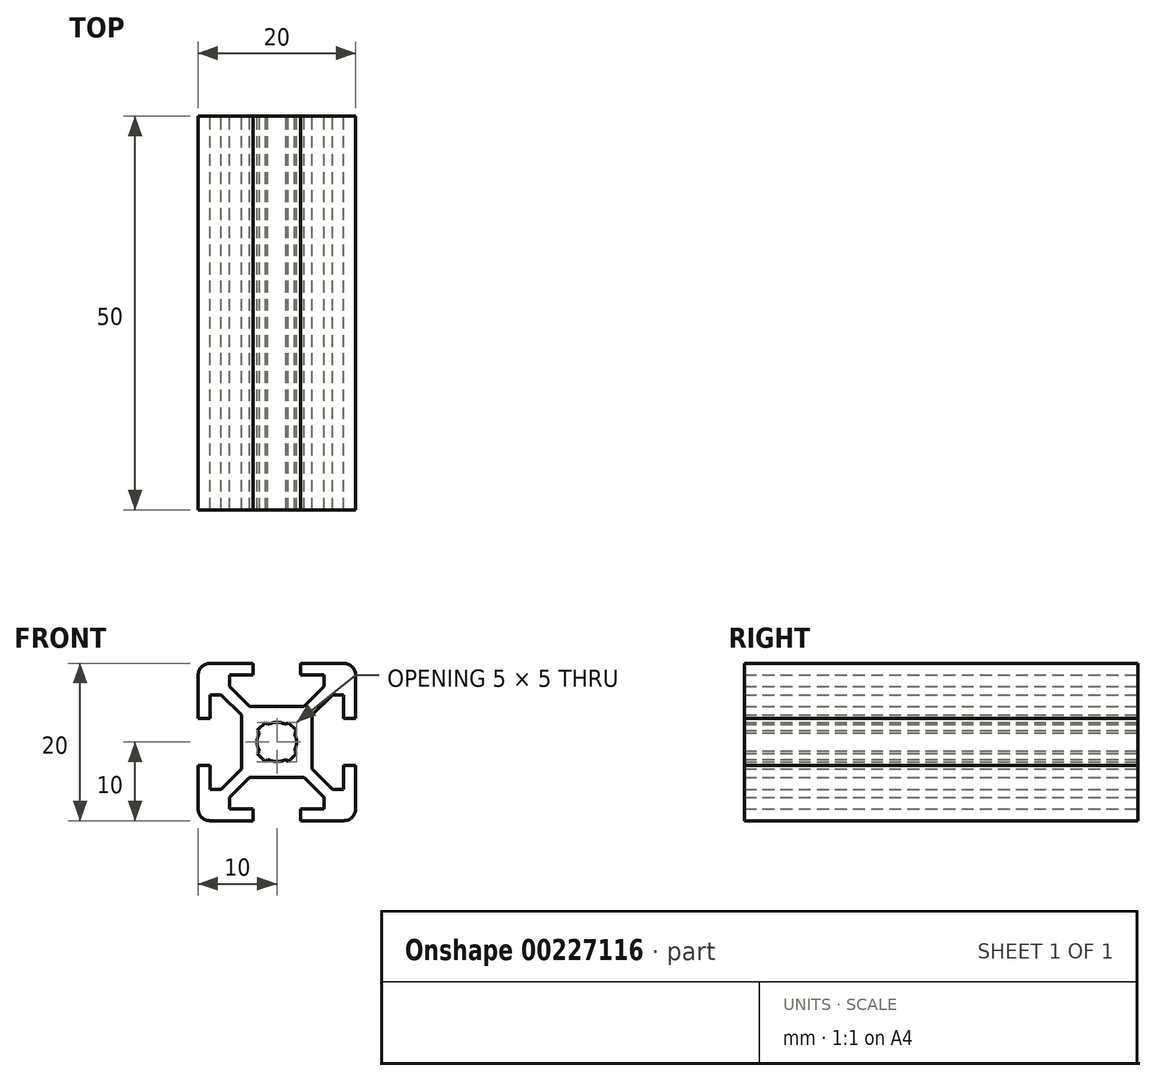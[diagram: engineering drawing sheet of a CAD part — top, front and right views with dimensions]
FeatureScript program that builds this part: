
annotation { "Feature Type Name" : "Feature", "Feature Type Description" : "" }
export const myFeature = defineFeature(function(context is Context, id is Id, definition is map)
    precondition{}
    {
        {
            var Q0;
            Q0=qCreatedBy(makeId("Front.planeOp"),FACE);
            var sketch = newSketch(context, id + "F0", { "sketchPlane" : qUnion([Q0])});
            skLineSegment(sketch, "E0.bottom", {"start": v(8.5, -10) * mm, "end": v(3, -10) * mm});
            skLineSegment(sketch, "E0.top", {"start": v(8.5, 10) * mm, "end": v(3, 10) * mm});
            skLineSegment(sketch, "E0.left", {"start": v(10, -8.5) * mm, "end": v(10, -3) * mm});
            skLineSegment(sketch, "E0.right", {"start": v(-10, -8.5) * mm, "end": v(-10, -3) * mm});
            skPoint(sketch, "E0.middle", {"position": v(0, 0) * mm});
            skLineSegment(sketch, "E1.bottom", {"start": v(6, -8.5) * mm, "end": v(3, -8.5) * mm});
            skLineSegment(sketch, "E1.top", {"start": v(6, 8.5) * mm, "end": v(3, 8.5) * mm});
            skLineSegment(sketch, "E1.left", {"start": v(8.5, -6) * mm, "end": v(8.5, -3) * mm});
            skLineSegment(sketch, "E1.right", {"start": v(-8.5, -6) * mm, "end": v(-8.5, -3) * mm});
            skLineSegment(sketch, "E2.bottom", {"start": v(3.44, -4.5) * mm, "end": v(-3.44, -4.5) * mm});
            skLineSegment(sketch, "E2.top", {"start": v(3.44, 4.5) * mm, "end": v(-3.44, 4.5) * mm});
            skLineSegment(sketch, "E2.left", {"start": v(4.5, -3.44) * mm, "end": v(4.5, 3.44) * mm});
            skLineSegment(sketch, "E2.right", {"start": v(-4.5, -3.44) * mm, "end": v(-4.5, 3.44) * mm});
            skLineSegment(sketch, "E3.bottom", {"start": v(8.5, -6) * mm, "end": v(7.06, -6) * mm});
            skLineSegment(sketch, "E3.top", {"start": v(8.5, 6) * mm, "end": v(7.06, 6) * mm});
            skLineSegment(sketch, "E4.left", {"start": v(6, -8.5) * mm, "end": v(6, -7.06) * mm});
            skLineSegment(sketch, "E4.right", {"start": v(-6, -8.5) * mm, "end": v(-6, -7.06) * mm});
            skPoint(sketch, "E5.orphan", {"position": v(-8.5, 8.5) * mm});
            skPoint(sketch, "E6.orphan", {"position": v(8.5, 8.5) * mm});
            skPoint(sketch, "E7.orphan", {"position": v(8.5, -8.5) * mm});
            skPoint(sketch, "E8.orphan", {"position": v(-8.5, -8.5) * mm});
            skLineSegment(sketch, "E9.trimOffspring", {"start": v(-6, 7.06) * mm, "end": v(-6, 8.5) * mm});
            skLineSegment(sketch, "E10.trimOffspring", {"start": v(-7.06, 6) * mm, "end": v(-8.5, 6) * mm});
            skLineSegment(sketch, "E11.trimOffspring", {"start": v(6, 7.06) * mm, "end": v(6, 8.5) * mm});
            skLineSegment(sketch, "E12.trimOffspring", {"start": v(-7.06, -6) * mm, "end": v(-8.5, -6) * mm});
            skLineSegment(sketch, "E13", {"start": v(-10, 10) * mm, "end": v(0, 0) * mm, "construction": true});
            skLineSegment(sketch, "E14", {"start": v(10, 10) * mm, "end": v(0, 0) * mm, "construction": true});
            skLineSegment(sketch, "E15", {"start": v(-6, 7.06) * mm, "end": v(-3.44, 4.5) * mm});
            skPoint(sketch, "E15.endSnap0", {"position": v(7.25, -6) * mm});
            skLineSegment(sketch, "E16", {"start": v(6, -7.06) * mm, "end": v(3.44, -4.5) * mm});
            skLineSegment(sketch, "E17", {"start": v(7.06, 6) * mm, "end": v(4.5, 3.44) * mm});
            skLineSegment(sketch, "E18", {"start": v(6, 7.06) * mm, "end": v(3.44, 4.5) * mm});
            skPoint(sketch, "E19.orphan", {"position": v(6, -6) * mm});
            skPoint(sketch, "E20.orphan", {"position": v(-4.5, -4.5) * mm});
            skPoint(sketch, "E21.orphan", {"position": v(-4.5, 4.5) * mm});
            skPoint(sketch, "E22.orphan", {"position": v(4.5, 4.5) * mm});
            skPoint(sketch, "E23.orphan", {"position": v(4.5, -4.5) * mm});
            skLineSegment(sketch, "E24.trimOffspring", {"start": v(4.5, -3.44) * mm, "end": v(7.06, -6) * mm});
            skLineSegment(sketch, "E25.trimOffspring", {"start": v(-3.44, -4.5) * mm, "end": v(-6, -7.06) * mm});
            skLineSegment(sketch, "E26.trimOffspring", {"start": v(-4.5, -3.44) * mm, "end": v(-7.06, -6) * mm});
            skLineSegment(sketch, "E27.trimOffspring", {"start": v(-4.5, 3.44) * mm, "end": v(-7.06, 6) * mm});
            skLineSegment(sketch, "E28.bottom", {"start": v(8.5, -3) * mm, "end": v(10, -3) * mm});
            skLineSegment(sketch, "E28.top", {"start": v(8.5, 3) * mm, "end": v(10, 3) * mm});
            skPoint(sketch, "E28.middle", {"position": v(10, 0) * mm});
            skLineSegment(sketch, "E29.left", {"start": v(3, 8.5) * mm, "end": v(3, 10) * mm});
            skLineSegment(sketch, "E29.right", {"start": v(-3, 8.5) * mm, "end": v(-3, 10) * mm});
            skPoint(sketch, "E29.middle", {"position": v(0, 10) * mm});
            skLineSegment(sketch, "E30.bottom", {"start": v(-8.5, 3) * mm, "end": v(-10, 3) * mm});
            skLineSegment(sketch, "E30.top", {"start": v(-8.5, -3) * mm, "end": v(-10, -3) * mm});
            skPoint(sketch, "E30.middle", {"position": v(-10, 0) * mm});
            skLineSegment(sketch, "E31.left", {"start": v(3, -8.5) * mm, "end": v(3, -10) * mm});
            skLineSegment(sketch, "E31.right", {"start": v(-3, -8.5) * mm, "end": v(-3, -10) * mm});
            skPoint(sketch, "E31.middle", {"position": v(0, -10) * mm});
            skPoint(sketch, "E32.orphan", {"position": v(3, 11.5) * mm});
            skPoint(sketch, "E33.orphan", {"position": v(-3, 11.5) * mm});
            skLineSegment(sketch, "E34.trimOffspring", {"start": v(-3, 10) * mm, "end": v(-8.5, 10) * mm});
            skLineSegment(sketch, "E35.trimOffspring", {"start": v(-3, 8.5) * mm, "end": v(-6, 8.5) * mm});
            skPoint(sketch, "E28.right.end.orphan", {"position": v(11.5, 3) * mm});
            skPoint(sketch, "E36.orphan", {"position": v(11.5, -3) * mm});
            skLineSegment(sketch, "E37.trimOffspring", {"start": v(10, 3) * mm, "end": v(10, 8.5) * mm});
            skLineSegment(sketch, "E38.trimOffspring", {"start": v(8.5, 3) * mm, "end": v(8.5, 6) * mm});
            skPoint(sketch, "E39.orphan", {"position": v(3, -11.5) * mm});
            skPoint(sketch, "E40.orphan", {"position": v(-3, -11.5) * mm});
            skLineSegment(sketch, "E41.trimOffspring", {"start": v(-3, -10) * mm, "end": v(-8.5, -10) * mm});
            skLineSegment(sketch, "E42.trimOffspring", {"start": v(-3, -8.5) * mm, "end": v(-6, -8.5) * mm});
            skPoint(sketch, "E30.right.end.orphan", {"position": v(-11.5, -3) * mm});
            skPoint(sketch, "E43.orphan", {"position": v(-11.5, 3) * mm});
            skLineSegment(sketch, "E44.trimOffspring", {"start": v(-10, 3) * mm, "end": v(-10, 8.5) * mm});
            skLineSegment(sketch, "E45.trimOffspring", {"start": v(-8.5, 3) * mm, "end": v(-8.5, 6) * mm});
            skLineSegment(sketch, "E46.trimOffspring", {"start": v(0, 0) * mm, "end": v(10, -10) * mm, "construction": true});
            skLineSegment(sketch, "E47.trimOffspring", {"start": v(0, 0) * mm, "end": v(-10, -10) * mm, "construction": true});
            skArc(sketch, "E48", {"start": v(1.16, 2.22) * mm, "mid": v(0, 2.5) * mm, "end": v(-1.16, 2.22) * mm});
            skLineSegment(sketch, "E49", {"start": v(-2.5, -1.44) * mm, "end": v(1.44, 2.5) * mm});
            skLineSegment(sketch, "E50", {"start": v(2.5, 1.44) * mm, "end": v(-1.44, -2.5) * mm});
            skLineSegment(sketch, "E51", {"start": v(1.44, -2.5) * mm, "end": v(-2.5, 1.44) * mm});
            skLineSegment(sketch, "E52", {"start": v(-1.44, 2.5) * mm, "end": v(2.5, -1.44) * mm});
            skLineSegment(sketch, "E53", {"start": v(2.5, 1.44) * mm, "end": v(2.5, -1.44) * mm, "construction": true});
            skLineSegment(sketch, "E54", {"start": v(1.44, -2.5) * mm, "end": v(-1.44, -2.5) * mm, "construction": true});
            skLineSegment(sketch, "E55", {"start": v(-2.5, -1.44) * mm, "end": v(-2.5, 1.44) * mm, "construction": true});
            skLineSegment(sketch, "E56", {"start": v(-1.44, 2.5) * mm, "end": v(1.44, 2.5) * mm, "construction": true});
            skLineSegment(sketch, "E57", {"start": v(-1.44, 2.5) * mm, "end": v(-2.5, 1.44) * mm});
            skLineSegment(sketch, "E58", {"start": v(1.44, 2.5) * mm, "end": v(2.5, 1.44) * mm});
            skLineSegment(sketch, "E59", {"start": v(2.5, -1.44) * mm, "end": v(1.44, -2.5) * mm});
            skLineSegment(sketch, "E60", {"start": v(-1.44, -2.5) * mm, "end": v(-2.5, -1.44) * mm});
            skArc(sketch, "E61.trimOffspring", {"start": v(-2.22, 1.16) * mm, "mid": v(-2.5, 0) * mm, "end": v(-2.22, -1.16) * mm});
            skArc(sketch, "E62.trimOffspring", {"start": v(-1.16, -2.22) * mm, "mid": v(0, -2.5) * mm, "end": v(1.16, -2.22) * mm});
            skArc(sketch, "E63.trimOffspring", {"start": v(2.22, -1.16) * mm, "mid": v(2.5, 0) * mm, "end": v(2.22, 1.16) * mm});
            skPoint(sketch, "E64.visualSharp", {"position": v(10, 10) * mm});
            skArc(sketch, "E64.filletArc", {"start": v(10, 8.5) * mm, "mid": v(9.56, 9.56) * mm, "end": v(8.5, 10) * mm});
            skPoint(sketch, "E65.visualSharp", {"position": v(10, -10) * mm});
            skArc(sketch, "E65.filletArc", {"start": v(8.5, -10) * mm, "mid": v(9.56, -9.56) * mm, "end": v(10, -8.5) * mm});
            skPoint(sketch, "E66.visualSharp", {"position": v(-10, -10) * mm});
            skArc(sketch, "E66.filletArc", {"start": v(-10, -8.5) * mm, "mid": v(-9.56, -9.56) * mm, "end": v(-8.5, -10) * mm});
            skPoint(sketch, "E67.visualSharp", {"position": v(-10, 10) * mm});
            skArc(sketch, "E67.filletArc", {"start": v(-8.5, 10) * mm, "mid": v(-9.56, 9.56) * mm, "end": v(-10, 8.5) * mm});
            skSolve(sketch);
        }
        {
            assignVariable(context, id + "F2", {"name" : "Length", "anyValue" : 50});
        }
        {
            var Q0;
            Q0=qSketchRegion(id+"F0",true);
            extrude(context, id + "F1", {"entities" : qUnion([Q0]), "depth" : (getVariable(context, 'Length')) * mm});
        }
    });
